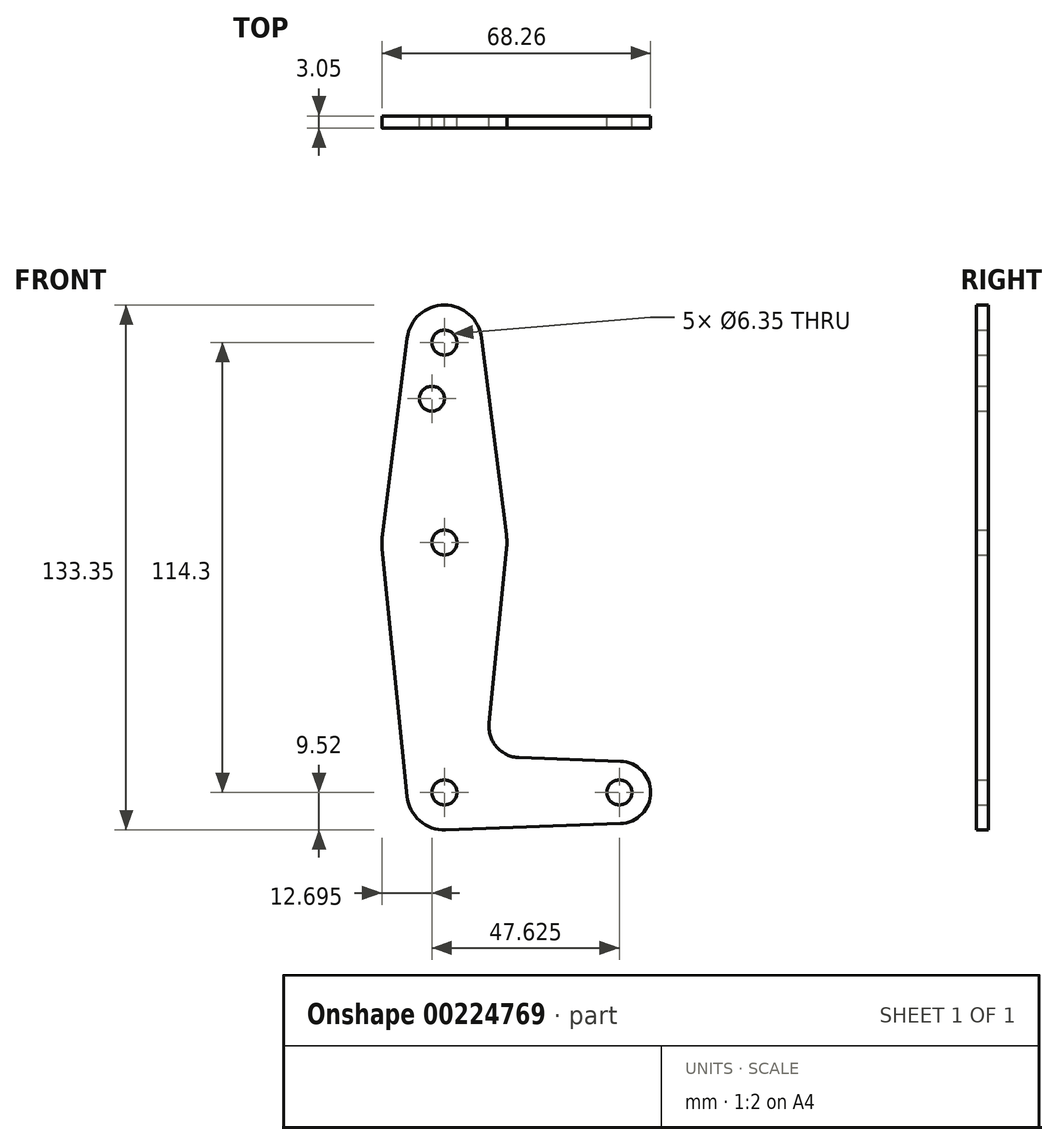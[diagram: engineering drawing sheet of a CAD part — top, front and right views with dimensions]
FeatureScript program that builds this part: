
annotation { "Feature Type Name" : "Feature", "Feature Type Description" : "" }
export const myFeature = defineFeature(function(context is Context, id is Id, definition is map)
    precondition{}
    {
        {
            var Q0;
            Q0=qCreatedBy(makeId("Front.planeOp"),FACE);
            var sketch = newSketch(context, id + "F0", { "sketchPlane" : qUnion([Q0])});
            skCircle(sketch, "E0", {"center": v(0, 0) * mm, "radius": 9.53 * mm});
            skLineSegment(sketch, "E1", {"start": v(0, 0) * mm, "end": v(0, 63.5) * mm, "construction": true});
            skLineSegment(sketch, "E2", {"start": v(0, 63.5) * mm, "end": v(0, 114.3) * mm, "construction": true});
            skLineSegment(sketch, "E3", {"start": v(0, 0) * mm, "end": v(44.45, 0) * mm});
            skCircle(sketch, "E4", {"center": v(0, 63.5) * mm, "radius": 15.88 * mm});
            skCircle(sketch, "E5", {"center": v(0, 114.3) * mm, "radius": 9.53 * mm});
            skCircle(sketch, "E6", {"center": v(44.45, 0) * mm, "radius": 7.94 * mm});
            skLineSegment(sketch, "E7", {"start": v(-9.45, 115.5) * mm, "end": v(-15.75, 65.48) * mm});
            skLineSegment(sketch, "E8", {"start": v(-15.8, 61.91) * mm, "end": v(-9.48, -0.95) * mm});
            skLineSegment(sketch, "E9", {"start": v(9.45, 115.5) * mm, "end": v(15.75, 65.48) * mm});
            skLineSegment(sketch, "E10", {"start": v(15.8, 61.91) * mm, "end": v(11.34, 17.6) * mm});
            skLineSegment(sketch, "E11", {"start": v(18.97, 8.85) * mm, "end": v(44.73, 7.93) * mm});
            skLineSegment(sketch, "E12", {"start": v(44.73, -7.93) * mm, "end": v(0.34, -9.52) * mm});
            skCircle(sketch, "E13", {"center": v(0, 114.3) * mm, "radius": 3.18 * mm});
            skCircle(sketch, "E14", {"center": v(-3.18, 100.03) * mm, "radius": 3.18 * mm});
            skCircle(sketch, "E15", {"center": v(0, 63.5) * mm, "radius": 3.18 * mm});
            skCircle(sketch, "E16", {"center": v(0, 0) * mm, "radius": 3.18 * mm});
            skCircle(sketch, "E17", {"center": v(44.45, 0) * mm, "radius": 3.18 * mm});
            skArc(sketch, "E18.filletArc", {"start": v(11.34, 17.6) * mm, "mid": v(13.26, 11.57) * mm, "end": v(18.97, 8.85) * mm});
            skSolve(sketch);
        }
        {
            var Q0;
            Q0 = qSketchRegion(id + "F0", true);
            extrude(context, id + "F1", {"entities" : qUnion([Q0]), "depth" : 3.05 * mm});
        }
    });
